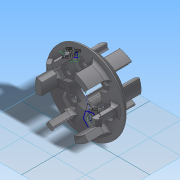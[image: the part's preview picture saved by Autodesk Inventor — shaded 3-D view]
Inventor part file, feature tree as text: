
AUTODESK INVENTOR PART (.ipt)
format: ipt  version: 2014 SP2 (Build 180246200, 246)  size: 1,103,872 bytes
history: native  units: in
note: dims shown in document units (in); Inventor stores cm internally (conversion verified against a paired STEP export)
features: reference x24, sketch x9, extrude x7, fillet x6, pattern_circular x4, sweep x1, chamfer x1, hole x1, boolean_combine x1
ambient origin geometry x8: Origin, YZ Plane, XZ Plane, XY Plane, X Axis, Y Axis, Z Axis, Center Point
bodies: Solid1 (feature_tree), Solid2 (feature_tree), Solid3 (feature_tree)
feature tree (54):
  extrude  "HookArm"  Depth=0.25in TaperAngle=45.0deg
  sweep  "Hook"
  extrude  "Extrusion11"  Depth=0.02in
  pattern_circular  "3xHooks"  [2 undecoded]
  extrude  "Spacer"  Depth=0.025in
  chamfer  "Chamfer1"  Distance=0.6709in
  extrude  "Spoke"  Depth=0.1in
  extrude  "Center Hole"  Depth=0.185in
  fillet  "Fillet7"  [1 undecoded]
  fillet  "Fillet8"  Radius=1.1811in
  fillet  "Fillet9"  Radius=0.025in
  fillet  "Fillet11"  Radius=0.025in
  sketch  "Sketch15"  dims[d72=0.01in]
  sketch  "Sketch17"  dims[d73=0.025in d74=0.025in d76=0.025in d77=0.6709in d78=0.0in d90=0.1in d94=0.185in d95=0.0in d96=1.1811in d97=360.0deg d99=0.025in d100=0.025in d101=0.025in d102=0.025in d103=0.5906in d104=0.0in d105=45.0deg d106=90.0deg d107=0.1in d108=0.055in d109=0.425in d110=0.225in d111=0.75in d112=0.375in d113=0.25in d114=0.5635in d115=1.0in d116=0.8108in d117=0.125in d118=0.0in d119=0.13in d120=0.0in d121=2.3622in d122=360.0deg d124=2.3622in d125=360.0deg d127=0.125in]
  extrude  "Extrusion12"  Depth=0.025in
  extrude  "Extrusion13"  Depth=0.025in
  hole  "Hole2"  [1 undecoded]
  pattern_circular  "Circular Pattern3"  Angle=45.0deg  [1 undecoded]
  pattern_circular  "Circular Pattern5"  Angle=90.0deg  [1 undecoded]
  pattern_circular  "Circular Pattern6"  [2 undecoded]
  boolean_combine  "Combine2"
  fillet  "Hooks Attach Fillet"  Radius=0.055in
  fillet  "Spoke Attach Fillet"  Radius=0.425in
  sketch  "Sketch2"  dims[d2=0.29in d3=0.0in d4=0.25in d5=0.25in d6=45.0deg]
  sketch  "Sketch5"  dims[d12=0.58in d13=0.0in d35=0.65in d36=0.0in]
  sketch  "Sketch9"  dims[d37=1.0in d38=1.0in d49=2.3622in d50=360.0deg d65=0.02in]
  reference  "Reference40"
  reference  "Reference41"
  reference  "Reference42"
  reference  "Reference43"
  reference  "Reference44"
  reference  "Reference45"
  reference  "Reference46"
  reference  "Reference47"
  reference  "Reference48"
  reference  "Reference49"
  reference  "Reference50"
  reference  "Reference51"
  reference  "Reference52"
  reference  "Reference53"
  sketch  "Sketch11"  dims[d66=0.02in]
  reference  "Reference54"
  reference  "Reference55"
  reference  "Reference56"
  reference  "Reference57"
  reference  "Reference58"
  sketch  "Sketch13"  dims[d69=0.01in]
  sketch  "3D Sketch2"
  sketch  "Sketch14"  dims[d71=0.025in]
  reference  "Reference59"
  reference  "Reference60"
  reference  "Reference61"
  reference  "Reference62"
  reference  "Reference63"
note: 8 required parameter values undecoded (feature->parameter linkage not recoverable at this tier; creation-order binding heuristic only, values carry confidence <= 0.55)
